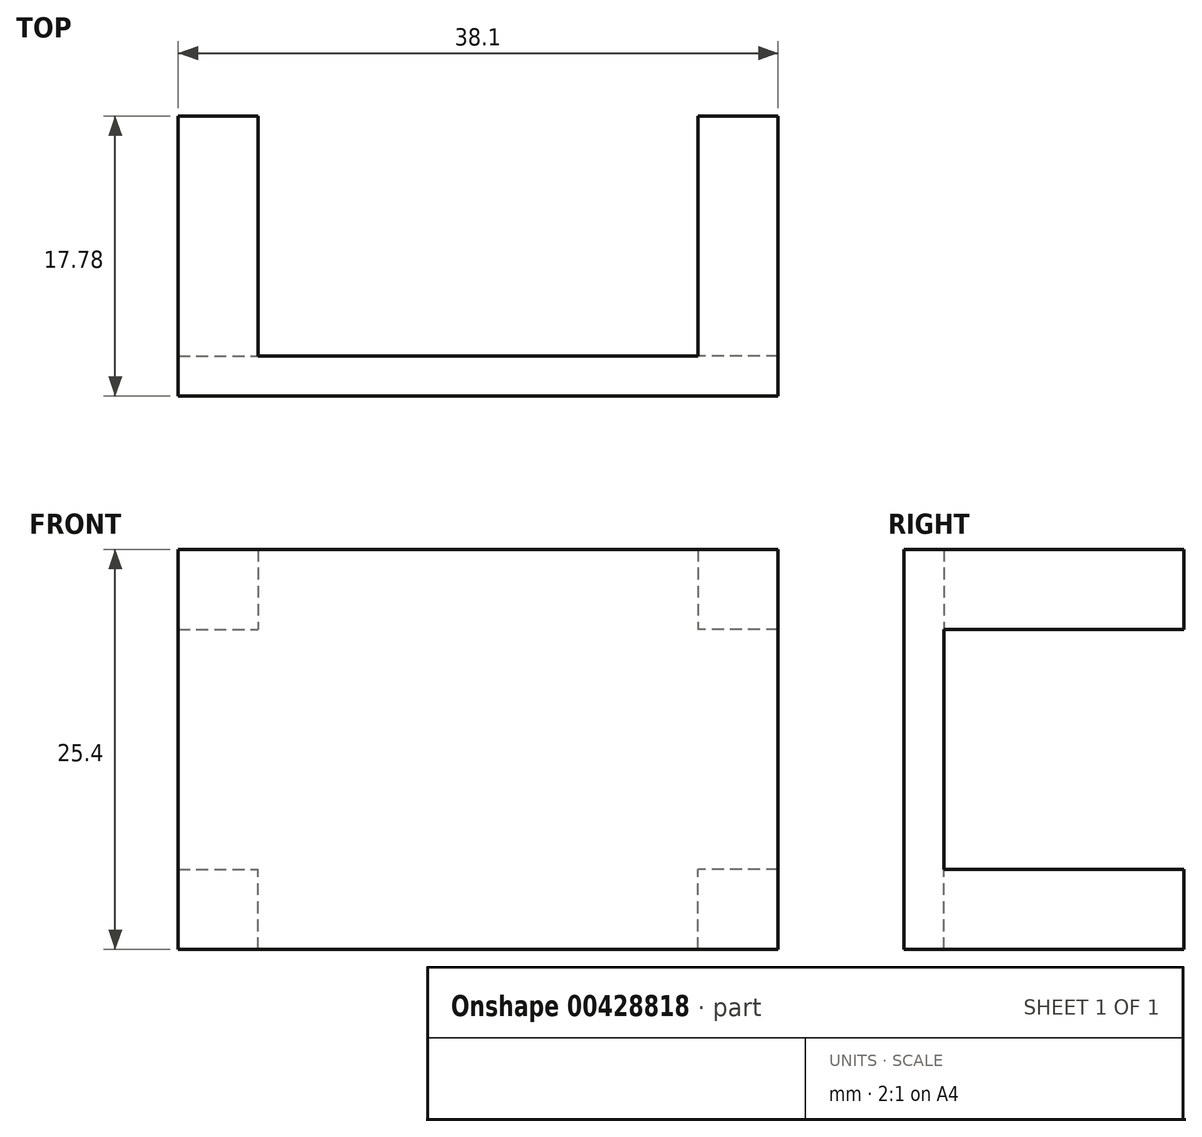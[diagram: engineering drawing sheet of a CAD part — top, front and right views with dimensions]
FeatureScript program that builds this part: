
annotation { "Feature Type Name" : "Feature", "Feature Type Description" : "" }
export const myFeature = defineFeature(function(context is Context, id is Id, definition is map)
    precondition{}
    {
        {
            var Q0;
            Q0=qCreatedBy(makeId("Front.planeOp"),FACE);
            var sketch = newSketch(context, id + "F0", { "sketchPlane" : qUnion([Q0])});
            skLineSegment(sketch, "E0.bottom", {"start": v(0, 0) * mm, "end": v(38.1, 0) * mm});
            skLineSegment(sketch, "E0.top", {"start": v(0, -25.4) * mm, "end": v(38.1, -25.4) * mm});
            skLineSegment(sketch, "E0.left", {"start": v(0, 0) * mm, "end": v(0, -25.4) * mm});
            skLineSegment(sketch, "E0.right", {"start": v(38.1, 0) * mm, "end": v(38.1, -25.4) * mm});
            skSolve(sketch);
        }
        {
            var Q0;
            Q0 = qSketchRegion(id + "F0", true);
            extrude(context, id + "F1", {"entities" : qUnion([Q0]), "depth" : 2.54 * mm});
        }
        {
            var Q0;
            Q0=makeQuery(id+"F1.opExtrude","CAP_FACE",FACE,{"disambiguationData":[OSD([sQuery(id+"F0.wireOp",EDGE,"E0.bottom"),sQuery(id+"F0.wireOp",EDGE,"E0.top"),sQuery(id+"F0.wireOp",EDGE,"E0.left"),sQuery(id+"F0.wireOp",EDGE,"E0.right")])],"isStart":true});
            var sketch = newSketch(context, id + "F2", { "sketchPlane" : qUnion([Q0])});
            skLineSegment(sketch, "E1.bottom", {"start": v(-38.1, 0) * mm, "end": v(-33.02, 0) * mm});
            skLineSegment(sketch, "E1.top", {"start": v(-38.1, -5.08) * mm, "end": v(-33.02, -5.08) * mm});
            skLineSegment(sketch, "E1.left", {"start": v(-38.1, 0) * mm, "end": v(-38.1, -5.08) * mm});
            skLineSegment(sketch, "E1.right", {"start": v(-33.02, 0) * mm, "end": v(-33.02, -5.08) * mm});
            skLineSegment(sketch, "E2.bottom", {"start": v(-38.1, -25.4) * mm, "end": v(-33.02, -25.4) * mm});
            skLineSegment(sketch, "E2.top", {"start": v(-38.1, -20.32) * mm, "end": v(-33.02, -20.32) * mm});
            skLineSegment(sketch, "E2.left", {"start": v(-38.1, -25.4) * mm, "end": v(-38.1, -20.32) * mm});
            skLineSegment(sketch, "E2.right", {"start": v(-33.02, -25.4) * mm, "end": v(-33.02, -20.32) * mm});
            skLineSegment(sketch, "E3.bottom", {"start": v(0, 0) * mm, "end": v(-5.08, 0) * mm});
            skLineSegment(sketch, "E3.top", {"start": v(0, -5.08) * mm, "end": v(-5.08, -5.08) * mm});
            skLineSegment(sketch, "E3.left", {"start": v(0, 0) * mm, "end": v(0, -5.08) * mm});
            skLineSegment(sketch, "E3.right", {"start": v(-5.08, 0) * mm, "end": v(-5.08, -5.08) * mm});
            skLineSegment(sketch, "E4.bottom", {"start": v(0, -25.4) * mm, "end": v(-5.08, -25.4) * mm});
            skLineSegment(sketch, "E4.top", {"start": v(0, -20.32) * mm, "end": v(-5.08, -20.32) * mm});
            skLineSegment(sketch, "E4.left", {"start": v(0, -25.4) * mm, "end": v(0, -20.32) * mm});
            skLineSegment(sketch, "E4.right", {"start": v(-5.08, -25.4) * mm, "end": v(-5.08, -20.32) * mm});
            skSolve(sketch);
        }
        {
            var Q0;
            Q0 = qSketchRegion(id + "F2", true);
            extrude(context, id + "F3", {"entities" : qUnion([Q0]), "operationType" : NewBodyOperationType.ADD, "depth" : 15.24 * mm});
        }
    });
